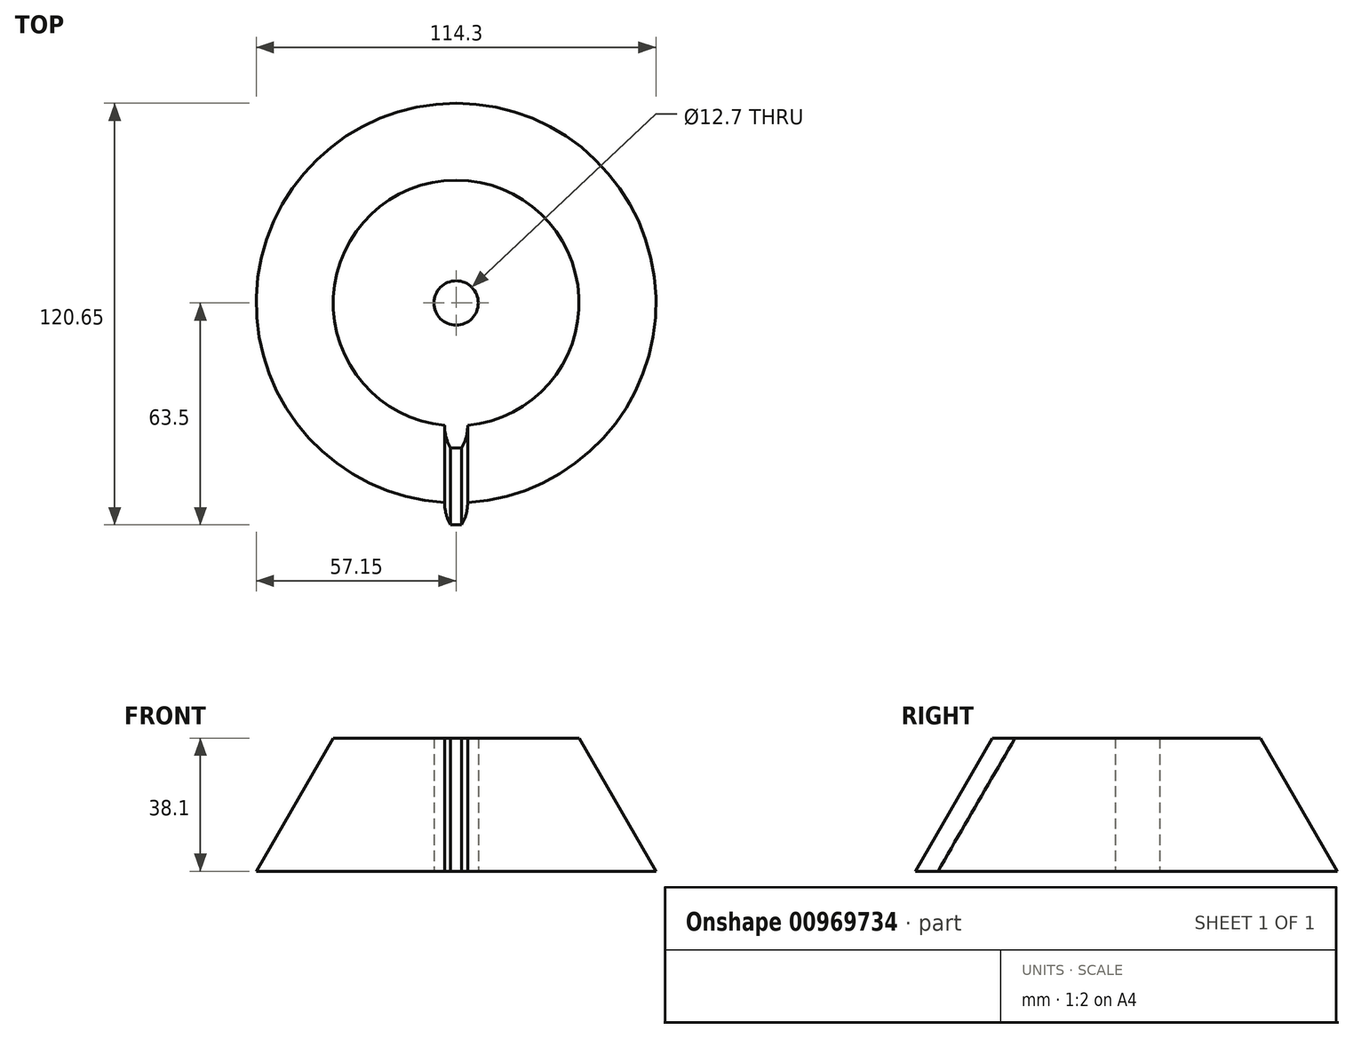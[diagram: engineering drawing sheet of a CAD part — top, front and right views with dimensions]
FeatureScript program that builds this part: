
annotation { "Feature Type Name" : "Feature", "Feature Type Description" : "" }
export const myFeature = defineFeature(function(context is Context, id is Id, definition is map)
    precondition{}
    {
        {
            var Q0;
            Q0=qCreatedBy(makeId("Front.planeOp"),FACE);
            var sketch = newSketch(context, id + "F0", { "sketchPlane" : qUnion([Q0])});
            skLineSegment(sketch, "E0", {"start": v(6.35, 38.1) * mm, "end": v(6.35, 0) * mm});
            skLineSegment(sketch, "E1", {"start": v(6.35, 0) * mm, "end": v(57.15, 0) * mm});
            skLineSegment(sketch, "E2", {"start": v(57.15, 0) * mm, "end": v(35.15, 38.1) * mm});
            skLineSegment(sketch, "E3", {"start": v(35.15, 38.1) * mm, "end": v(6.35, 38.1) * mm});
            skLineSegment(sketch, "E4", {"start": v(0, 0) * mm, "end": v(0, 68.51) * mm, "construction": true});
            skSolve(sketch);
        }
        {
            var Q0;
            Q0=makeQuery(id+"F0.imprint","IMPRINT",FACE,{"disambiguationData":[TD([[makeQuery(id+"F0.imprint","IMPRINT",EDGE,{"derivedFrom":sQuery(id+"F0.wireOp",EDGE,"E0")}),1.0]])]});
            var Q1;
            Q1=sQuery(id+"F0.wireOp",EDGE,"E4");
            revolve(context, id + "F1", {"surfaceOperationType" : NewSurfaceOperationType.NEW, "entities" : qUnion([Q0]), "axis" : qUnion([Q1]), "revolveType" : RevolveType.FULL});
        }
        {
            var Q0;
            Q0=makeQuery(id+"F1.opRevolve","SWEPT_FACE",FACE,{"disambiguationData":[OSD([sQuery(id+"F0.wireOp",EDGE,"E3")])]});
            var sketch = newSketch(context, id + "F2", { "sketchPlane" : qUnion([Q0])});
            skLineSegment(sketch, "E5", {"start": v(0, -41.5) * mm, "end": v(1.59, -41.5) * mm});
            skArc(sketch, "E6", {"start": v(1.59, -41.5) * mm, "mid": v(2.88, -38.37) * mm, "end": v(3.29, -35) * mm});
            skLineSegment(sketch, "E7", {"start": v(0, -41.5) * mm, "end": v(0, -35.15) * mm});
            skArc(sketch, "E8", {"start": v(3.29, -35) * mm, "mid": v(1.65, -35.11) * mm, "end": v(0, -35.15) * mm});
            skLineSegment(sketch, "E9.MirrorCS", {"start": v(0, -41.5) * mm, "end": v(-1.59, -41.5) * mm});
            skArc(sketch, "E10.MirrorCS", {"start": v(-1.59, -41.5) * mm, "mid": v(-2.88, -38.37) * mm, "end": v(-3.29, -35) * mm});
            skArc(sketch, "E11.MirrorCS", {"start": v(-3.29, -35) * mm, "mid": v(-1.65, -35.11) * mm, "end": v(0, -35.15) * mm});
            skSolve(sketch);
        }
        {
            var Q0;
            Q0=qCreatedBy(makeId("Right.planeOp"),FACE);
            var sketch = newSketch(context, id + "F3", { "sketchPlane" : qUnion([Q0])});
            skLineSegment(sketch, "E12", {"start": v(-57.15, 0) * mm, "end": v(-35.15, 38.1) * mm});
            skLineSegment(sketch, "E13", {"start": v(35.15, 38.1) * mm, "end": v(57.15, 0) * mm});
            skSolve(sketch);
        }
        {
            var Q0;
            Q0=makeQuery(id+"F2.imprint","IMPRINT",FACE,{"disambiguationData":[TD([[makeQuery(id+"F2.imprint","IMPRINT",EDGE,{"derivedFrom":sQuery(id+"F2.wireOp",EDGE,"E7")}),1.0]])]});
            var Q1;
            Q1=makeQuery(id+"F2.imprint","IMPRINT",FACE,{"disambiguationData":[TD([[makeQuery(id+"F2.imprint","IMPRINT",EDGE,{"derivedFrom":sQuery(id+"F2.wireOp",EDGE,"E5")}),1.0]])]});
            var Q2;
            Q2=sQuery(id+"F3.wireOp",EDGE,"E12");
            sweep(context, id + "F4", {"operationType" : NewBodyOperationType.ADD, "profiles" : qUnion([Q0, Q1]), "path" : qUnion([Q2])});
        }
    });
